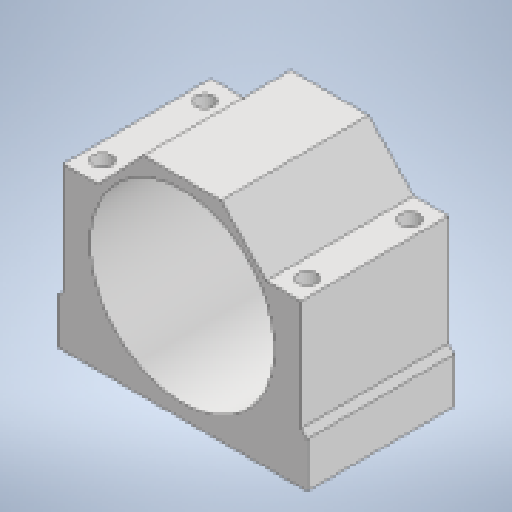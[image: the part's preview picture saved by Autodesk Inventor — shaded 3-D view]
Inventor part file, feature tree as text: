
AUTODESK INVENTOR PART (.ipt)
format: ipt  version: 2023 (Build 270158000, 158)  size: 162,816 bytes
history: native  units: mm
features: extrude x2, sketch x2
ambient origin geometry x8: Origin, YZ Plane, XZ Plane, XY Plane, X Axis, Y Axis, Z Axis, Center Point
bodies: Solid1 (feature_tree)
feature tree (4):
  extrude  "Extrusion1"  Depth=122.0mm
  extrude  "Extrusion2"  Depth=72.0mm
  sketch  "Sketch1"  dims[d0=79.0mm d1=122.0mm]
  sketch  "Sketch2"  dims[d2=52.0mm d3=90.0mm d4=17.0mm d5=38.0mm d6=102.0mm d7=116.0mm d8=135.0deg d9=72.0mm d10=0.0mm d11=100.0mm d12=50.0mm d13=9.0mm d14=72.0mm d15=0.0mm]
